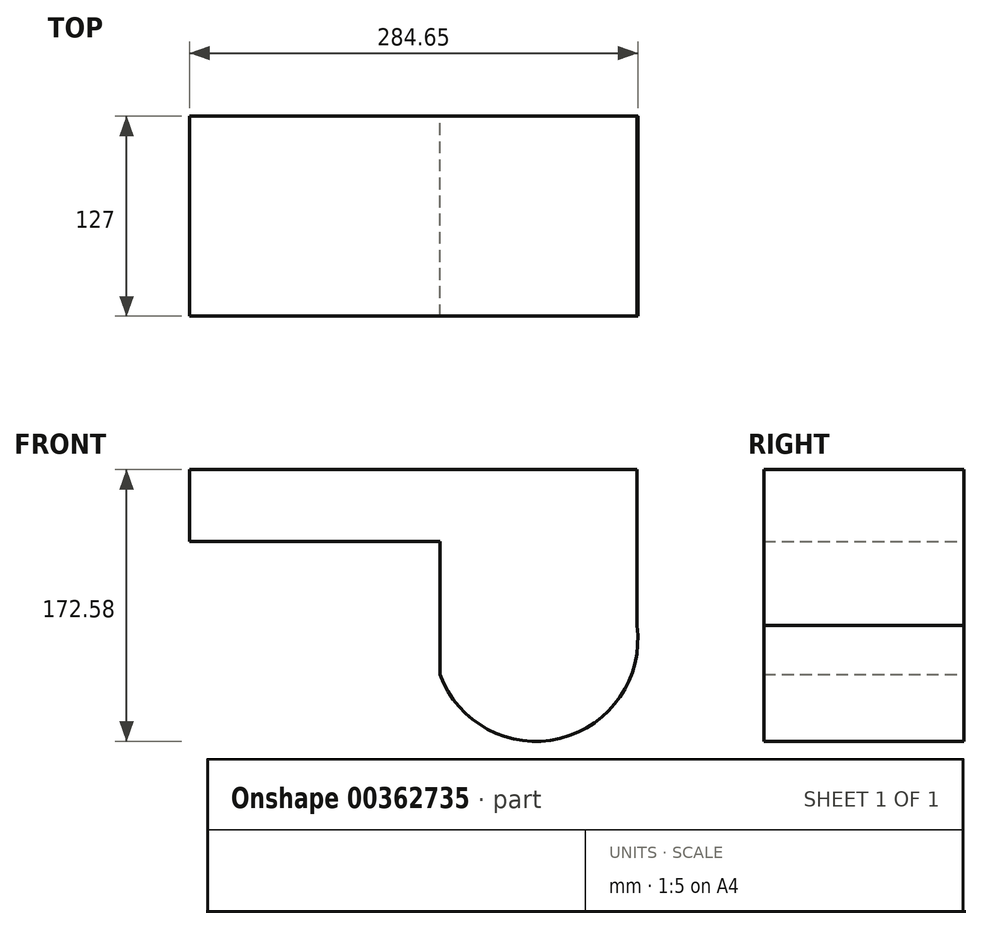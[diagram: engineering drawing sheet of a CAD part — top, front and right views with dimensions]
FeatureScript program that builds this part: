
annotation { "Feature Type Name" : "Feature", "Feature Type Description" : "" }
export const myFeature = defineFeature(function(context is Context, id is Id, definition is map)
    precondition{}
    {
        {
            var Q0;
            Q0=qCreatedBy(makeId("Front.planeOp"),FACE);
            var sketch = newSketch(context, id + "F0", { "sketchPlane" : qUnion([Q0])});
            skLineSegment(sketch, "E0.bottom", {"start": v(0, 80.86) * mm, "end": v(149.39, 80.86) * mm});
            skLineSegment(sketch, "E0.top", {"start": v(0, -18.26) * mm, "end": v(149.39, -18.26) * mm});
            skLineSegment(sketch, "E0.left", {"start": v(0, 80.86) * mm, "end": v(0, -18.26) * mm});
            skLineSegment(sketch, "E0.right", {"start": v(149.39, 80.86) * mm, "end": v(149.39, -18.26) * mm});
            skLineSegment(sketch, "E1.bottom", {"start": v(24.19, 35.33) * mm, "end": v(-134.69, 35.33) * mm});
            skLineSegment(sketch, "E1.top", {"start": v(24.19, -49.08) * mm, "end": v(-134.69, -49.08) * mm});
            skLineSegment(sketch, "E1.left", {"start": v(24.19, 35.33) * mm, "end": v(24.19, -49.08) * mm});
            skLineSegment(sketch, "E1.right", {"start": v(-134.69, 35.33) * mm, "end": v(-134.69, -49.08) * mm});
            skArc(sketch, "E2", {"start": v(24.19, -49.08) * mm, "mid": v(100.62, -89.84) * mm, "end": v(149.39, -18.26) * mm});
            skLineSegment(sketch, "E3.bottom", {"start": v(0, 80.86) * mm, "end": v(-134.69, 80.86) * mm});
            skLineSegment(sketch, "E3.top", {"start": v(0, 35.33) * mm, "end": v(-134.69, 35.33) * mm});
            skLineSegment(sketch, "E3.left", {"start": v(0, 80.86) * mm, "end": v(0, 35.33) * mm});
            skLineSegment(sketch, "E3.right", {"start": v(-134.69, 80.86) * mm, "end": v(-134.69, 35.33) * mm});
            skSolve(sketch);
        }
        {
            var Q0;
            Q0=makeQuery(id+"F0.imprint","IMPRINT",FACE,{"disambiguationData":[TD([[makeQuery(id+"F0.imprint","IMPRINT",EDGE,{"derivedFrom":sQuery(id+"F0.wireOp",EDGE,"E3.bottom")}),1.0]])]});
            var Q1;
            {var subQ4=sQuery(id+"F0.wireOp",EDGE,"E0.left");Q1=makeQuery(id+"F0.imprint","IMPRINT",FACE,{"disambiguationData":[TD([[makeQuery(id+"F0.imprint","IMPRINT",EDGE,{"derivedFrom":subQ4}),-1.0]])]});}
            var Q2;
            {var subQ0=sQuery(id+"F0.wireOp",EDGE,"E2");Q2=makeQuery(id+"F0.imprint","IMPRINT",FACE,{"disambiguationData":[TD([[makeQuery(id+"F0.imprint","IMPRINT",EDGE,{"derivedFrom":subQ0}),1.0]])]});}
            var Q3;
            Q3=makeQuery(id+"F0.imprint","IMPRINT",FACE,{"disambiguationData":[TD([[makeQuery(id+"F0.imprint","IMPRINT",EDGE,{"derivedFrom":sQuery(id+"F0.wireOp",EDGE,"E0.bottom")}),-1.0]])]});
            extrude(context, id + "F1", {"entities" : qUnion([Q0, Q1, Q2, Q3]), "depth" : 127 * mm});
        }
    });
